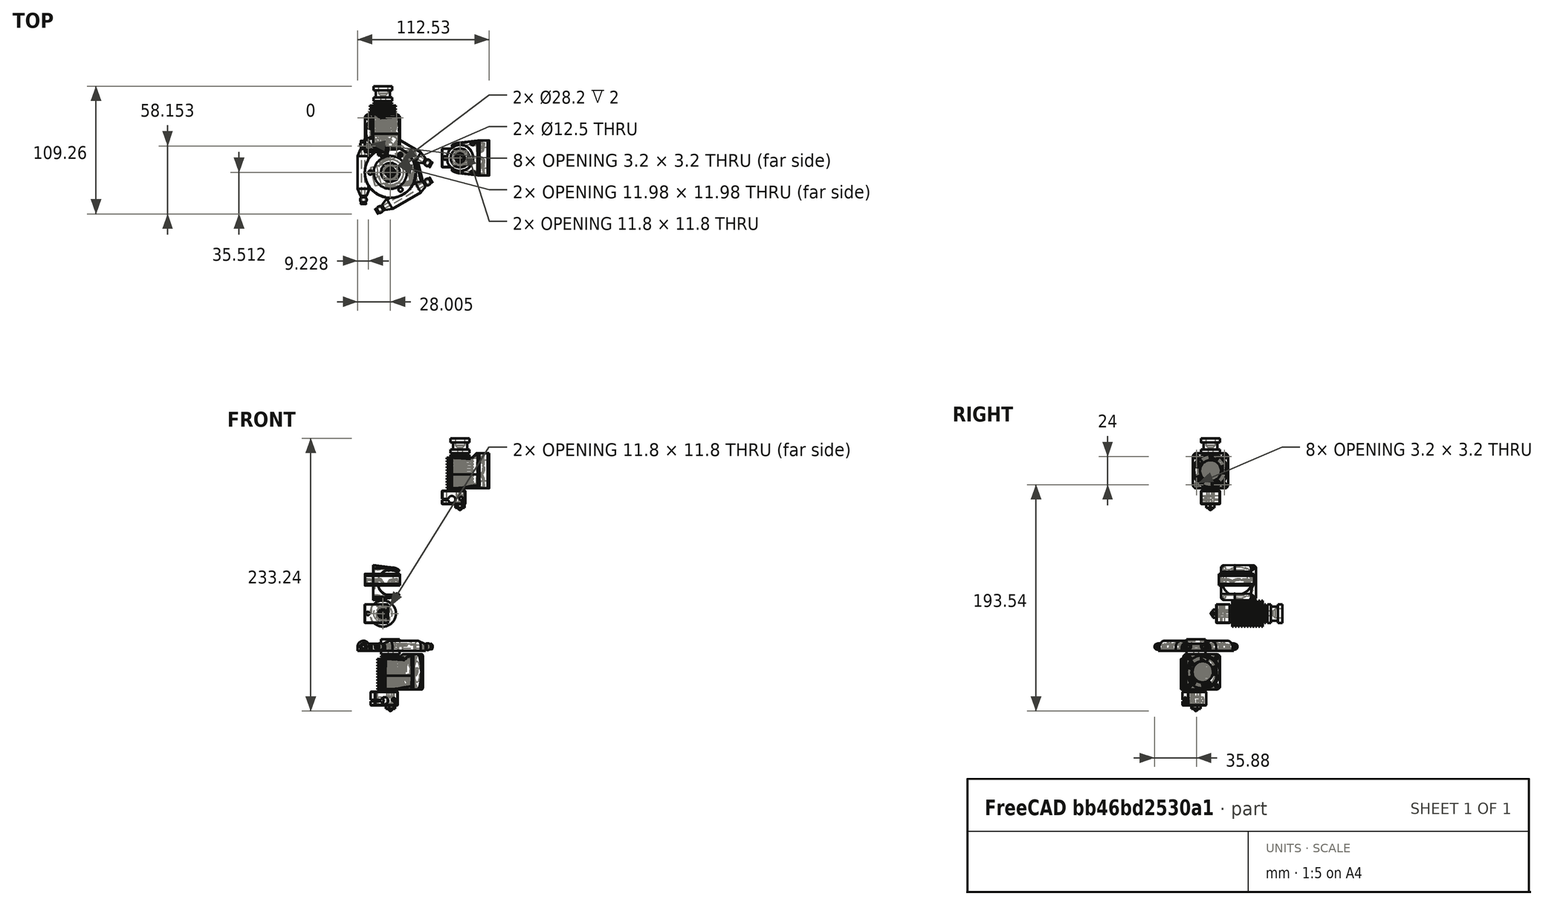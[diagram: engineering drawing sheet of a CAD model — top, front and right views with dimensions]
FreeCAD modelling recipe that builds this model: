
FCSTD DOCUMENT  (FreeCAD 2022.430R26244 +4758 (Git))
Label: As3DeltaEffector
License: All rights reserved
LicenseURL: http://en.wikipedia.org/wiki/All_rights_reserved
objects: Part::FeaturePython×30, App::FeaturePython×27, Part::Feature×9, App::LinkElement×6, App::Part×3, App::Link×2
note: 37 computed .brp shape members not serialized (recipe doc carries the construction recipe); baked Part::Feature solids carry a one-line shape summary decoded from their .brp
EXTERNAL_REF file=As3Traxxas5347BallJoint.FCStd obj=Assembly

FEATURE [App::FeaturePython] Constraints001  # WARN: FeaturePython — macro-defined, semantics opaque (R4)
  TreeRank = 258
  _LinkVersion = 1
  _Version = 1
FEATURE [Part::Feature] Solid  label="e3d nozzle (0.4)"
  Placement = pos=(0,-4.25,4e-16) rot=(0,0,1;0rad)
  TreeRank = 195
  shape: bbox 8.083 x 12.5 x 7 mm, 31 faces (baked)
FEATURE [Part::Feature] Solid001  label="e3d heaterblock"
  Placement = pos=(-5.5,-1.25,6.9e-15) rot=(0,0,1;0rad)
  TreeRank = 196
  shape: bbox 20 x 11.5 x 16 mm, 45 faces (baked)
FEATURE [Part::Feature] Solid002  label="e3d heat break"
  Placement = pos=(0,5.25,4e-16) rot=(0,0,1;0rad)
  TreeRank = 197
  shape: bbox 7 x 21.9 x 7 mm, 23 faces (baked)
FEATURE [Part::Feature] Solid003  label="e3d heatsink"
  Placement = pos=(0,12.35,4e-16) rot=(0,1,0;0.209118rad)
  TreeRank = 198
  shape: bbox 22.3 x 42.7 x 22.3 mm, 92 faces (baked)
FEATURE [Part::Feature] Solid004  label="fan duct"
  Placement = pos=(6.82793,2.62156,26.4875) rot=(0,0,1;0rad)
  TreeRank = 199
  shape: bbox 55.54 x 30 x 38.08 mm, 106 faces (baked)
FEATURE [Part::Feature] Solid005  label="fan sub1"
  Placement = pos=(-0.402046,15.9429,23.9537) rot=(0,0,1;0rad)
  TreeRank = 200
  shape: bbox 30 x 30 x 10 mm, 57 faces (baked)
FEATURE [Part::Feature] Solid006  label="fan sub2"
  Placement = pos=(-0.402046,15.9429,33.9537) rot=(-0.381664,-0.841822,-0.381664;1.74214rad)
  TreeRank = 201
  shape: bbox 29.15 x 29.85 x 8.5 mm, 30 faces (baked)
FEATURE [App::Part] Part  label="fan"
  ClaimAllChildren = false
  ExportMode = 1
  Group = -> [Solid005,Solid006]
  Origin = -> Origin001
  Placement = pos=(15.7816,1.67867,26.8895) rot=(0,-1,0;1.5708rad)
  TreeRank = 203
  _ExportChildren = -> [Solid005,Solid006]
  _GroupVersion = 1
FEATURE [App::Part] Part001  label="fanduct"
  ClaimAllChildren = false
  ExportMode = 1
  Group = -> [Solid004,Part]
  Origin = -> Origin002
  Placement = pos=(6.82793,9.72844,26.4875) rot=(0,1,0;3.14159rad)
  TreeRank = 205
  _ExportChildren = -> [Solid004,Part]
  _GroupVersion = 1
FEATURE [App::Part] Part002  label="e3d v6"
  ClaimAllChildren = false
  ExportMode = 1
  Group = -> [Solid,Solid001,Solid002,Solid003,Part001]
  Origin = -> Origin003
  Placement = pos=(65.8913,-6.33526,94.8) rot=(1,0.000157,0.000157;1.5708rad)
  TreeRank = 207
  _ExportChildren = -> [Solid,Solid001,Solid002,Solid003,Part001]
  _GroupVersion = 1
FEATURE [Part::FeaturePython] Parts001  # WARN: FeaturePython — macro-defined, semantics opaque (R4)
  Group = -> [Part002]
  GroupMode = 0
  TreeRank = 260
  _LinkVersion = 1
FEATURE [App::Link] Link001  label="AsE3dv007"
  AutoLinkLabel = false
  AutoPlacement = true
  LinkPlacement = pos=(-59.0731,-28.6152,-171.944) rot=(0,0,1;0.246235rad)
  LinkedObject = -> Assembly001
  Placement = pos=(-59.0731,-28.6152,-171.944) rot=(0,0,1;0.246235rad)
  SyncGroupVisibility = false
  TreeRank = 0
  _LinkOwner = 965
  _LinkVersion = 1
FEATURE [Part::Feature] Part__Feature044  label="Delta Effector"
  Placement = pos=(-5.1086,-20.3772,-4.35843) rot=(0,0,1;1.13446rad)
  TreeRank = 0
  shape: bbox 58.07 x 64.17 x 8.5 mm, 53 faces (baked)
FEATURE [App::LinkElement] Link_i0
  LinkPlacement = pos=(-16.625,-42.188,-28.294) rot=(0,0,-1;1.5708rad)
  LinkedObject = -> <external As3Traxxas5347BallJoint.FCStd>#Assembly
  Placement = pos=(-16.625,-42.188,-28.294) rot=(0,0,-1;1.5708rad)
  TreeRank = 265
  _LinkOwner = 548
  _LinkVersion = 1
FEATURE [App::LinkElement] Link_i1
  LinkPlacement = pos=(-16.625,4.79197,-28.294) rot=(0,0,-1;4.71239rad)
  LinkedObject = -> <external As3Traxxas5347BallJoint.FCStd>#Assembly
  Placement = pos=(-16.625,4.79197,-28.294) rot=(0,0,-1;4.71239rad)
  TreeRank = 266
  _LinkOwner = 548
  _LinkVersion = 1
FEATURE [App::LinkElement] Link_i2
  LinkPlacement = pos=(-2.46794,12.9656,-28.294) rot=(0,0,-1;3.66519rad)
  LinkedObject = -> <external As3Traxxas5347BallJoint.FCStd>#Assembly
  Placement = pos=(-2.46794,12.9656,-28.294) rot=(0,0,-1;3.66519rad)
  TreeRank = 267
  _LinkOwner = 548
  _LinkVersion = 1
FEATURE [App::LinkElement] Link_i3
  LinkPlacement = pos=(38.2179,-10.5244,-28.294) rot=(0,0,-1;0.523599rad)
  LinkedObject = -> <external As3Traxxas5347BallJoint.FCStd>#Assembly
  Placement = pos=(38.2179,-10.5244,-28.294) rot=(0,0,-1;0.523599rad)
  TreeRank = 268
  _LinkOwner = 548
  _LinkVersion = 1
FEATURE [App::LinkElement] Link_i4
  LinkPlacement = pos=(38.2179,-26.8716,-28.294) rot=(0,0,1;0.523599rad)
  LinkedObject = -> <external As3Traxxas5347BallJoint.FCStd>#Assembly
  Placement = pos=(38.2179,-26.8716,-28.294) rot=(0,0,1;0.523599rad)
  TreeRank = 269
  _LinkOwner = 548
  _LinkVersion = 1
FEATURE [App::LinkElement] Link_i5
  LinkPlacement = pos=(-2.46794,-50.3616,-28.294) rot=(0,0,-1;2.61799rad)
  LinkedObject = -> <external As3Traxxas5347BallJoint.FCStd>#Assembly
  Placement = pos=(-2.46794,-50.3616,-28.294) rot=(0,0,-1;2.61799rad)
  TreeRank = 270
  _LinkOwner = 548
  _LinkVersion = 1
FEATURE [App::Link] Link  label="As3Traxxas5347ball"
  AutoLinkLabel = false
  AutoPlacement = true
  ElementCount = 6
  ElementList = -> [Link_i0,Link_i1,Link_i2,Link_i3,Link_i4,Link_i5]
  LinkedObject = -> <external As3Traxxas5347BallJoint.FCStd>#Assembly
  SyncGroupVisibility = false
  TreeRank = 264
  _LinkOwner = 534
  _LinkVersion = 1
FEATURE [Part::FeaturePython] Parts002  # WARN: FeaturePython — macro-defined, semantics opaque (R4)
  Group = -> [Part__Feature044,Link001,Link]
  GroupMode = 0
  TreeRank = 0
  _LinkVersion = 1
FEATURE [Part::Feature] Solid007  label="5347 ball"
  TreeRank = 285
  shape: bbox 6.98 x 5.77 x 5.77 mm, 10 faces (baked)
FEATURE [Part::FeaturePython] Assembly001  label="AsE3dv6"  # WARN: FeaturePython — macro-defined, semantics opaque (R4)
  AutoRelax = true
  BuildShape = 0
  Freeze = true
  Group = -> [Constraints001,Elements001,Parts001]
  TreeRank = 261
  Verbose = false
  _LinkVersion = 1
  _SolverType = 1
  _Version = 1
FEATURE [App::FeaturePython] Elements001  # WARN: FeaturePython — macro-defined, semantics opaque (R4)
  Group = -> [Element005]
  TreeRank = 259
  _LinkVersion = 1
FEATURE [Part::FeaturePython] Assembly002  label="As3DeltaEffector"  # WARN: FeaturePython — macro-defined, semantics opaque (R4)
  AutoRelax = true
  BuildShape = 0
  Freeze = true
  Group = -> [Constraints002,Elements002,Parts002]
  TreeRank = 263
  Verbose = false
  _LinkVersion = 1
  _SolverType = 1
  _Version = 1
FEATURE [App::FeaturePython] Constraint  label="Locked"  # WARN: FeaturePython — macro-defined, semantics opaque (R4)
  Disabled = false
  Group = -> [ElementLink]
  TreeRank = 0
  _ConstraintType = 0
  _LinkVersion = 1
  _Parent = -> Constraints002
FEATURE [App::FeaturePython] Constraint001  label="PlaneCoincident"  # WARN: FeaturePython — macro-defined, semantics opaque (R4)
  Angle = 0
  AnglePitch = 0
  AngleRoll = 0
  Cascade = false
  Disabled = false
  Group = -> [ElementLink001,ElementLink002]
  LockAngle = false
  Multiply = false
  OffsetX = 0
  OffsetY = 0
  TreeRank = 0
  _ConstraintType = 35
  _LinkVersion = 1
  _Parent = -> Constraints002
FEATURE [App::FeaturePython] Constraint002  label="PlaneCoincident001"  # WARN: FeaturePython — macro-defined, semantics opaque (R4)
  Angle = 0
  AnglePitch = 0
  AngleRoll = 0
  Cascade = false
  Disabled = false
  Group = -> [ElementLink003,ElementLink004]
  LockAngle = false
  Multiply = false
  OffsetX = 0
  OffsetY = 0
  TreeRank = 0
  _ConstraintType = 35
  _LinkVersion = 1
  _Parent = -> Constraints002
FEATURE [App::FeaturePython] Constraint003  label="PlaneCoincident002"  # WARN: FeaturePython — macro-defined, semantics opaque (R4)
  Angle = 0
  AnglePitch = 0
  AngleRoll = 0
  Cascade = false
  Disabled = false
  Group = -> [ElementLink005,ElementLink006]
  LockAngle = false
  Multiply = false
  OffsetX = 0
  OffsetY = 0
  TreeRank = 0
  _ConstraintType = 35
  _LinkVersion = 1
  _Parent = -> Constraints002
FEATURE [App::FeaturePython] Constraint004  label="PlaneCoincident003"  # WARN: FeaturePython — macro-defined, semantics opaque (R4)
  Angle = 0
  AnglePitch = 0
  AngleRoll = 0
  Cascade = false
  Disabled = false
  Group = -> [ElementLink007,ElementLink008]
  LockAngle = false
  Multiply = false
  OffsetX = 0
  OffsetY = 0
  TreeRank = 0
  _ConstraintType = 35
  _LinkVersion = 1
  _Parent = -> Constraints002
FEATURE [App::FeaturePython] Constraint005  label="PlaneCoincident004"  # WARN: FeaturePython — macro-defined, semantics opaque (R4)
  Angle = 0
  AnglePitch = 0
  AngleRoll = 0
  Cascade = false
  Disabled = false
  Group = -> [ElementLink009,ElementLink010]
  LockAngle = false
  Multiply = false
  OffsetX = 0
  OffsetY = 0
  TreeRank = 0
  _ConstraintType = 35
  _LinkVersion = 1
  _Parent = -> Constraints002
FEATURE [App::FeaturePython] Constraint006  label="PlaneCoincident005"  # WARN: FeaturePython — macro-defined, semantics opaque (R4)
  Angle = 0
  AnglePitch = 0
  AngleRoll = 0
  Cascade = false
  Disabled = false
  Group = -> [ElementLink011,ElementLink012]
  LockAngle = false
  Multiply = false
  OffsetX = 0
  OffsetY = 0
  TreeRank = 0
  _ConstraintType = 35
  _LinkVersion = 1
  _Parent = -> Constraints002
FEATURE [App::FeaturePython] Constraints002  # WARN: FeaturePython — macro-defined, semantics opaque (R4)
  Group = -> [Constraint,Constraint001,Constraint002,Constraint003,Constraint004,Constraint005,Constraint006,Constraint007]
  TreeRank = 0
  _LinkVersion = 1
  _Version = 1
FEATURE [Part::FeaturePython] Element  label="ElSphereM@As3Traxxas5347ball@#3"  # link proxy (typed FeaturePython)
  Detach = false
  LinkTransform = true
  LinkedObject = -> Link [Link_i3.1.$ElSphereM.]
  TreeRank = 0
  _LinkVersion = 1
  _Parent = -> Elements002
FEATURE [Part::FeaturePython] Element004  label="Element001"  # link proxy (typed FeaturePython)
  Detach = false
  LinkTransform = true
  LinkedObject = -> Part__Feature044 [Face51]
  TreeRank = 0
  _LinkVersion = 1
  _Parent = -> Elements002
FEATURE [App::FeaturePython] ElementLink  label="_Element"  # link proxy (typed FeaturePython)
  LinkTransform = true
  LinkedObject = -> _Element
  TreeRank = 0
  _LinkVersion = 1
  _Parent = -> Constraint
FEATURE [App::FeaturePython] ElementLink001  label="ElCircle@As3Traxxas5347ball@#0"  # link proxy (typed FeaturePython)
  LinkTransform = true
  LinkedObject = -> _Element001
  TreeRank = 0
  _LinkVersion = 1
  _Parent = -> Constraint001
FEATURE [App::FeaturePython] ElementLink002  label="_Element002"  # link proxy (typed FeaturePython)
  LinkTransform = true
  LinkedObject = -> _Element002
  TreeRank = 0
  _LinkVersion = 1
  _Parent = -> Constraint001
FEATURE [App::FeaturePython] ElementLink003  label="ElCircle@As3Traxxas5347ball@#1"  # link proxy (typed FeaturePython)
  LinkTransform = true
  LinkedObject = -> _Element003
  TreeRank = 0
  _LinkVersion = 1
  _Parent = -> Constraint002
FEATURE [App::FeaturePython] ElementLink004  label="_Element004"  # link proxy (typed FeaturePython)
  LinkTransform = true
  LinkedObject = -> _Element004
  TreeRank = 0
  _LinkVersion = 1
  _Parent = -> Constraint002
FEATURE [App::FeaturePython] ElementLink005  label="ElCircle@As3Traxxas5347ball@#2"  # link proxy (typed FeaturePython)
  LinkTransform = true
  LinkedObject = -> _Element005
  TreeRank = 0
  _LinkVersion = 1
  _Parent = -> Constraint003
FEATURE [App::FeaturePython] ElementLink006  label="_Element006"  # link proxy (typed FeaturePython)
  LinkTransform = true
  LinkedObject = -> _Element006
  TreeRank = 0
  _LinkVersion = 1
  _Parent = -> Constraint003
FEATURE [App::FeaturePython] ElementLink007  label="ElCircle@As3Traxxas5347ball@#3"  # link proxy (typed FeaturePython)
  LinkTransform = true
  LinkedObject = -> _Element007
  TreeRank = 0
  _LinkVersion = 1
  _Parent = -> Constraint004
FEATURE [App::FeaturePython] ElementLink008  label="_Element008"  # link proxy (typed FeaturePython)
  LinkTransform = true
  LinkedObject = -> _Element008
  TreeRank = 0
  _LinkVersion = 1
  _Parent = -> Constraint004
FEATURE [App::FeaturePython] ElementLink009  label="ElCircle@As3Traxxas5347ball@#4"  # link proxy (typed FeaturePython)
  LinkTransform = true
  LinkedObject = -> _Element009
  TreeRank = 0
  _LinkVersion = 1
  _Parent = -> Constraint005
FEATURE [App::FeaturePython] ElementLink010  label="_Element010"  # link proxy (typed FeaturePython)
  LinkTransform = true
  LinkedObject = -> _Element010
  TreeRank = 0
  _LinkVersion = 1
  _Parent = -> Constraint005
FEATURE [App::FeaturePython] ElementLink011  label="ElCircle@As3Traxxas5347ball@#5"  # link proxy (typed FeaturePython)
  LinkTransform = true
  LinkedObject = -> _Element011
  TreeRank = 0
  _LinkVersion = 1
  _Parent = -> Constraint006
FEATURE [App::FeaturePython] ElementLink012  label="_Element012"  # link proxy (typed FeaturePython)
  LinkTransform = true
  LinkedObject = -> _Element012
  TreeRank = 0
  _LinkVersion = 1
  _Parent = -> Constraint006
FEATURE [App::FeaturePython] Elements002  # WARN: FeaturePython — macro-defined, semantics opaque (R4)
  Group = -> [_Element,_Element001,_Element002,_Element003,_Element004,_Element005,_Element006,_Element007,_Element008,_Element009,_Element010,_Element011,_Element012,Element,Element004,_Element013,_Element014,Element006,Element007,Element008,Element009,Element010,Element011,Element012,Element013]
  TreeRank = 0
  _LinkVersion = 1
FEATURE [Part::FeaturePython] _Element  # link proxy (typed FeaturePython)
  Detach = false
  LinkTransform = true
  LinkedObject = -> Part__Feature044 [Face50]
  TreeRank = 0
  _LinkVersion = 1
  _Parent = -> Elements002
FEATURE [Part::FeaturePython] _Element001  label="ElCircle@As3Traxxas5347ball@#0"  # link proxy (typed FeaturePython)
  Detach = false
  LinkTransform = true
  LinkedObject = -> Link [Link_i0.1.$ElCircle.]
  TreeRank = 0
  _LinkVersion = 1
  _Parent = -> Elements002
FEATURE [Part::FeaturePython] _Element002  # link proxy (typed FeaturePython)
  Detach = false
  LinkTransform = true
  LinkedObject = -> Part__Feature044 [Edge45]
  TreeRank = 0
  _LinkVersion = 1
  _Parent = -> Elements002
FEATURE [Part::FeaturePython] _Element003  label="ElCircle@As3Traxxas5347ball@#1"  # link proxy (typed FeaturePython)
  Detach = false
  LinkTransform = true
  LinkedObject = -> Link [Link_i1.1.$ElCircle.]
  TreeRank = 0
  _LinkVersion = 1
  _Parent = -> Elements002
FEATURE [Part::FeaturePython] _Element004  # link proxy (typed FeaturePython)
  Detach = false
  LinkTransform = true
  LinkedObject = -> Part__Feature044 [Edge44]
  TreeRank = 0
  _LinkVersion = 1
  _Parent = -> Elements002
FEATURE [Part::FeaturePython] _Element005  label="ElCircle@As3Traxxas5347ball@#2"  # link proxy (typed FeaturePython)
  Detach = false
  LinkTransform = true
  LinkedObject = -> Link [Link_i2.1.$ElCircle.]
  TreeRank = 0
  _LinkVersion = 1
  _Parent = -> Elements002
FEATURE [Part::FeaturePython] _Element006  # link proxy (typed FeaturePython)
  Detach = false
  LinkTransform = true
  LinkedObject = -> Part__Feature044 [Edge37]
  TreeRank = 0
  _LinkVersion = 1
  _Parent = -> Elements002
FEATURE [Part::FeaturePython] _Element007  label="ElCircle@As3Traxxas5347ball@#3"  # link proxy (typed FeaturePython)
  Detach = false
  LinkTransform = true
  LinkedObject = -> Link [Link_i3.1.$ElCircle.]
  TreeRank = 0
  _LinkVersion = 1
  _Parent = -> Elements002
FEATURE [Part::FeaturePython] _Element008  # link proxy (typed FeaturePython)
  Detach = false
  LinkTransform = true
  LinkedObject = -> Part__Feature044 [Edge36]
  TreeRank = 0
  _LinkVersion = 1
  _Parent = -> Elements002
FEATURE [Part::FeaturePython] _Element009  label="ElCircle@As3Traxxas5347ball@#4"  # link proxy (typed FeaturePython)
  Detach = false
  LinkTransform = true
  LinkedObject = -> Link [Link_i4.1.$ElCircle.]
  TreeRank = 0
  _LinkVersion = 1
  _Parent = -> Elements002
FEATURE [Part::FeaturePython] _Element010  # link proxy (typed FeaturePython)
  Detach = false
  LinkTransform = true
  LinkedObject = -> Part__Feature044 [Edge24]
  TreeRank = 0
  _LinkVersion = 1
  _Parent = -> Elements002
FEATURE [Part::FeaturePython] _Element011  label="ElCircle@As3Traxxas5347ball@#5"  # link proxy (typed FeaturePython)
  Detach = false
  LinkTransform = true
  LinkedObject = -> Link [Link_i5.1.$ElCircle.]
  TreeRank = 0
  _LinkVersion = 1
  _Parent = -> Elements002
FEATURE [Part::FeaturePython] _Element012  # link proxy (typed FeaturePython)
  Detach = false
  LinkTransform = true
  LinkedObject = -> Part__Feature044 [Edge23]
  TreeRank = 0
  _LinkVersion = 1
  _Parent = -> Elements002
FEATURE [App::FeaturePython] Constraint007  label="PlaneCoincident006"  # WARN: FeaturePython — macro-defined, semantics opaque (R4)
  Angle = 0
  AnglePitch = 0
  AngleRoll = 0
  Cascade = false
  Disabled = false
  Group = -> [ElementLink013,ElementLink014]
  LockAngle = false
  Multiply = false
  OffsetX = 0
  OffsetY = 0
  TreeRank = 271
  _ConstraintType = 35
  _LinkVersion = 1
  _Parent = -> Constraints002
FEATURE [App::FeaturePython] ElementLink013  label="_Element013"  # link proxy (typed FeaturePython)
  LinkTransform = true
  LinkedObject = -> _Element013
  TreeRank = 272
  _LinkVersion = 1
  _Parent = -> Constraint007
FEATURE [Part::FeaturePython] _Element013  # link proxy (typed FeaturePython)
  Detach = false
  LinkTransform = true
  LinkedObject = -> Part__Feature044 [Edge136]
  TreeRank = 273
  _LinkVersion = 1
  _Parent = -> Elements002
FEATURE [App::FeaturePython] ElementLink014  label="_Element014"  # link proxy (typed FeaturePython)
  LinkTransform = true
  LinkedObject = -> _Element014
  TreeRank = 274
  _LinkVersion = 1
  _Parent = -> Constraint007
FEATURE [Part::FeaturePython] Element005  # link proxy (typed FeaturePython)
  Detach = false
  LinkTransform = true
  LinkedObject = -> Part002 [Solid003.Edge147]
  TreeRank = 275
  _LinkVersion = 1
  _Parent = -> Elements001
FEATURE [Part::FeaturePython] _Element014  # link proxy (typed FeaturePython)
  Detach = false
  LinkTransform = true
  LinkedObject = -> Link001 [1.$Element005.]
  TreeRank = 276
  _LinkVersion = 1
  _Parent = -> Elements002
FEATURE [Part::FeaturePython] Element006  label="ElSphereM@As3Traxxas5347ball@#0"  # link proxy (typed FeaturePython)
  Detach = false
  LinkTransform = true
  LinkedObject = -> Link [Link_i0.1.$ElSphereM.]
  TreeRank = 277
  _LinkVersion = 1
  _Parent = -> Elements002
FEATURE [Part::FeaturePython] Element007  label="ElSphereM@As3Traxxas5347ball@#1"  # link proxy (typed FeaturePython)
  Detach = false
  LinkTransform = true
  LinkedObject = -> Link [Link_i1.1.$ElSphereM.]
  TreeRank = 278
  _LinkVersion = 1
  _Parent = -> Elements002
FEATURE [Part::FeaturePython] Element008  label="ElSphereM@As3Traxxas5347ball@#2"  # link proxy (typed FeaturePython)
  Detach = false
  LinkTransform = true
  LinkedObject = -> Link [Link_i2.1.$ElSphereM.]
  TreeRank = 279
  _LinkVersion = 1
  _Parent = -> Elements002
FEATURE [Part::FeaturePython] Element009  label="ElSphereM@As3Traxxas5347ball@#4"  # link proxy (typed FeaturePython)
  Detach = false
  LinkTransform = true
  LinkedObject = -> Link [Link_i4.1.$ElSphereM.]
  TreeRank = 280
  _LinkVersion = 1
  _Parent = -> Elements002
FEATURE [Part::FeaturePython] Element010  label="ElSphereM@As3Traxxas5347ball@#5"  # link proxy (typed FeaturePython)
  Detach = false
  LinkTransform = true
  LinkedObject = -> Link [Link_i5.1.$ElSphereM.]
  TreeRank = 281
  _LinkVersion = 1
  _Parent = -> Elements002
FEATURE [Part::FeaturePython] Element011  # link proxy (typed FeaturePython)
  Detach = false
  LinkTransform = true
  LinkedObject = -> Link [1.1.$Element007.]
  TreeRank = 282
  _LinkVersion = 1
  _Parent = -> Elements002
FEATURE [Part::FeaturePython] Element012  # link proxy (typed FeaturePython)
  Detach = false
  LinkTransform = true
  LinkedObject = -> Link [0.1.$Element007.]
  TreeRank = 283
  _LinkVersion = 1
  _Parent = -> Elements002
FEATURE [Part::FeaturePython] Element013  # link proxy (typed FeaturePython)
  Detach = false
  LinkTransform = true
  LinkedObject = -> Part__Feature044 [Edge135]
  TreeRank = 284
  _LinkVersion = 1
  _Parent = -> Elements002

RESOLVED EXTERNAL PARTS (link-assembly join: the EXTERNAL_REF files above that resolve inside this repo's crawl, each included once):
---- part As3Traxxas5347BallJoint.FCStd = doc fcstd_eef68f0d1be9 ----
FCSTD DOCUMENT  (FreeCAD 2022.430R26244 +4758 (Git))
Label: As3Traxxas5347BallJoint
License: All rights reserved
LicenseURL: http://en.wikipedia.org/wiki/All_rights_reserved
objects: Part::FeaturePython×13, App::FeaturePython×4, Part::Feature×2, Part::SubShapeBinder×1, PartDesign::Plane×1
note: 15 computed .brp shape members not serialized (recipe doc carries the construction recipe); baked Part::Feature solids carry a one-line shape summary decoded from their .brp

FEATURE [Part::Feature] Solid  label="5347 ball"
  TreeRank = 11
  shape: bbox 6.98 x 5.77 x 5.77 mm, 10 faces (baked)
FEATURE [Part::Feature] Solid001  label="rod end 5347"
  Placement = pos=(-0.00421036,0.0017498,0.0142902) rot=(0.550048,0.628407,0.550048;2.0195rad)
  TreeRank = 12
  shape: bbox 7.577 x 11.49 x 22.98 mm, 43 faces (baked)
FEATURE [App::FeaturePython] Constraints  # WARN: FeaturePython — macro-defined, semantics opaque (R4)
  TreeRank = 8
  _LinkVersion = 1
  _Version = 1
FEATURE [Part::FeaturePython] Parts  # WARN: FeaturePython — macro-defined, semantics opaque (R4)
  Group = -> [Solid]
  GroupMode = 0
  TreeRank = 10
  _LinkVersion = 1
FEATURE [App::FeaturePython] Constraints001  # WARN: FeaturePython — macro-defined, semantics opaque (R4)
  TreeRank = 16
  _LinkVersion = 1
  _Version = 1
FEATURE [Part::SubShapeBinder] Import  label="Import(rod end 5347)"
  BindCopyOnChange = 0
  BindMode = 0
  ClaimChildren = false
  FillStyle = 0
  Fuse = false
  MakeFace = false
  PartialLoad = false
  Relative = true
  Support = -> [Solid001]
  TreeRank = 27
  _Version = 8
FEATURE [PartDesign::Plane] DatumPlane
  AttachmentOffset = pos=(0,0,0) rot=(1,0,0;1.5708rad)
  Length = 10
  MapMode = 5
  MinimumLength = 10
  MinimumWidth = 10
  Placement = pos=(0,-2.29526,-17.183) rot=(1,0,0;4.5796rad)
  ResizeMode = 0
  Support = -> [Import]
  TreeRank = 26
  Width = 24.8985
FEATURE [Part::FeaturePython] Parts001  # WARN: FeaturePython — macro-defined, semantics opaque (R4)
  Group = -> [Solid001,DatumPlane,Import]
  GroupMode = 0
  TreeRank = 18
  _LinkVersion = 1
FEATURE [Part::FeaturePython] Assembly  label="As3Traxxas5347ball"  # WARN: FeaturePython — macro-defined, semantics opaque (R4)
  AutoRelax = true
  BuildShape = 0
  Freeze = false
  Group = -> [Constraints,Elements,Parts]
  TreeRank = 7
  Verbose = false
  _LinkVersion = 1
  _SolverType = 1
  _Version = 1
FEATURE [App::FeaturePython] Elements  # WARN: FeaturePython — macro-defined, semantics opaque (R4)
  Group = -> [Element001,Element003,Element007]
  TreeRank = 9
  _LinkVersion = 1
FEATURE [Part::FeaturePython] Element001  label="ElSphereM"  # link proxy (typed FeaturePython)
  Detach = false
  LinkTransform = true
  LinkedObject = -> Solid [Face8]
  TreeRank = 14
  _LinkVersion = 1
  _Parent = -> Elements
FEATURE [Part::FeaturePython] Assembly001  label="As3rodEnd5347"  # WARN: FeaturePython — macro-defined, semantics opaque (R4)
  AutoRelax = true
  BuildShape = 0
  Freeze = false
  Group = -> [Constraints001,Elements001,Parts001]
  TreeRank = 15
  Verbose = false
  _LinkVersion = 1
  _SolverType = 1
  _Version = 1
FEATURE [App::FeaturePython] Elements001  # WARN: FeaturePython — macro-defined, semantics opaque (R4)
  Group = -> [Element,Element002,Element004,Element005,Element006,Element008]
  TreeRank = 17
  _LinkVersion = 1
FEATURE [Part::FeaturePython] Element  label="ElSphereF"  # link proxy (typed FeaturePython)
  Detach = false
  LinkTransform = true
  LinkedObject = -> Solid001 [Face1]
  TreeRank = 19
  _LinkVersion = 1
  _Parent = -> Elements001
FEATURE [Part::FeaturePython] Element002  label="ElCircle1"  # link proxy (typed FeaturePython)
  Detach = false
  LinkTransform = true
  LinkedObject = -> Solid001 [Edge8]
  TreeRank = 20
  _LinkVersion = 1
  _Parent = -> Elements001
FEATURE [Part::FeaturePython] Element003  label="ElCircle"  # link proxy (typed FeaturePython)
  Detach = false
  LinkTransform = true
  LinkedObject = -> Solid [Edge10]
  TreeRank = 21
  _LinkVersion = 1
  _Parent = -> Elements
FEATURE [Part::FeaturePython] Element004  label="ElCircle2"  # link proxy (typed FeaturePython)
  Detach = false
  LinkTransform = true
  LinkedObject = -> Solid001 [Edge6]
  TreeRank = 22
  _LinkVersion = 1
  _Parent = -> Elements001
FEATURE [Part::FeaturePython] Element005  label="ElPlane"  # link proxy (typed FeaturePython)
  Detach = false
  LinkTransform = true
  LinkedObject = -> Solid001 [Face42]
  TreeRank = 23
  _LinkVersion = 1
  _Parent = -> Elements001
FEATURE [Part::FeaturePython] Element006  # link proxy (typed FeaturePython)
  Detach = false
  LinkTransform = true
  LinkedObject = -> Solid001 [Face32]
  TreeRank = 24
  _LinkVersion = 1
  _Parent = -> Elements001
FEATURE [Part::FeaturePython] Element007  # link proxy (typed FeaturePython)
  Detach = false
  LinkTransform = true
  LinkedObject = -> Solid [Face3]
  TreeRank = 25
  _LinkVersion = 1
  _Parent = -> Elements
FEATURE [Part::FeaturePython] Element008  label="ElSymSphF"  # link proxy (typed FeaturePython)
  Detach = false
  LinkTransform = true
  LinkedObject = -> DatumPlane
  TreeRank = 28
  _LinkVersion = 1
  _Parent = -> Elements001
